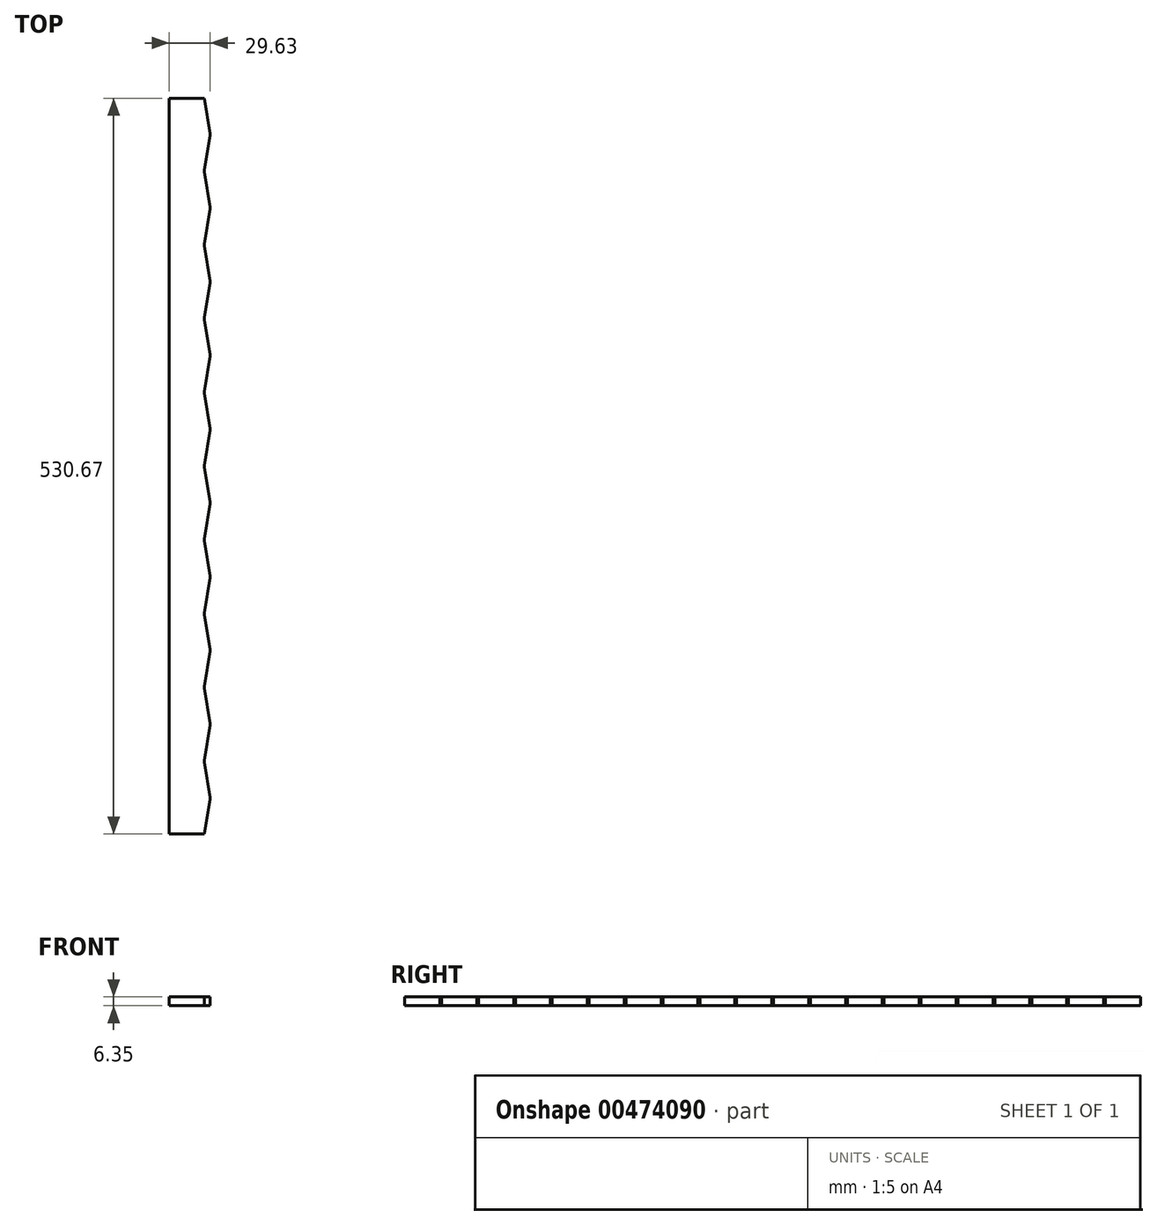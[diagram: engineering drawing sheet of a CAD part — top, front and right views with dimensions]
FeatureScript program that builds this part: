
annotation { "Feature Type Name" : "Feature", "Feature Type Description" : "" }
export const myFeature = defineFeature(function(context is Context, id is Id, definition is map)
    precondition{}
    {
        {
            var Q0;
            Q0=qCreatedBy(makeId("Top.planeOp"),FACE);
            var sketch = newSketch(context, id + "F0", { "sketchPlane" : qUnion([Q0])});
            skLineSegment(sketch, "E0.bottom", {"start": v(0, 0) * mm, "end": v(25.4, 0) * mm});
            skLineSegment(sketch, "E0.top", {"start": v(0, 530.67) * mm, "end": v(25.4, 530.67) * mm});
            skLineSegment(sketch, "E0.left", {"start": v(0, 0) * mm, "end": v(0, 530.67) * mm});
            skLineSegment(sketch, "E0.right", {"start": v(25.4, 0) * mm, "end": v(25.4, 530.67) * mm});
            skLineSegment(sketch, "E1", {"start": v(29.63, 25.3) * mm, "end": v(29.63, 26.6) * mm});
            skLineSegment(sketch, "E2.direction1", {"start": v(25.4, 0) * mm, "end": v(25.4, 51.9) * mm, "construction": true});
            skLineSegment(sketch, "E3", {"start": v(27.52, 39.25) * mm, "end": v(27.52, 12.65) * mm, "construction": true});
            skLineSegment(sketch, "E4", {"start": v(29.63, 25.95) * mm, "end": v(27.52, 25.95) * mm, "construction": true});
            skLineSegment(sketch, "E5", {"start": v(27.52, 25.95) * mm, "end": v(25.4, 25.95) * mm, "construction": true});
            skLineSegment(sketch, "E6", {"start": v(25.4, 51.9) * mm, "end": v(29.63, 26.6) * mm});
            skLineSegment(sketch, "E7", {"start": v(29.63, 25.3) * mm, "end": v(25.4, 0) * mm});
            skLineSegment(sketch, "E8", {"start": v(27.52, 12.65) * mm, "end": v(31.25, 12.03) * mm, "construction": true});
            skLineSegment(sketch, "E9.1.0.0", {"start": v(29.63, 78.5) * mm, "end": v(25.4, 53.2) * mm});
            skLineSegment(sketch, "E9.1.0.1", {"start": v(29.63, 78.5) * mm, "end": v(29.63, 79.8) * mm});
            skLineSegment(sketch, "E9.1.0.2", {"start": v(25.4, 105.1) * mm, "end": v(29.63, 79.8) * mm});
            skLineSegment(sketch, "E9.2.0.0", {"start": v(29.63, 131.7) * mm, "end": v(25.4, 106.4) * mm});
            skLineSegment(sketch, "E9.2.0.1", {"start": v(29.63, 131.7) * mm, "end": v(29.63, 133) * mm});
            skLineSegment(sketch, "E9.2.0.2", {"start": v(25.4, 158.3) * mm, "end": v(29.63, 133) * mm});
            skLineSegment(sketch, "E9.3.0.0", {"start": v(29.63, 184.9) * mm, "end": v(25.4, 159.59) * mm});
            skLineSegment(sketch, "E9.3.0.1", {"start": v(29.63, 184.9) * mm, "end": v(29.63, 186.19) * mm});
            skLineSegment(sketch, "E9.3.0.2", {"start": v(25.4, 211.5) * mm, "end": v(29.63, 186.19) * mm});
            skLineSegment(sketch, "E9.4.0.0", {"start": v(29.63, 238.1) * mm, "end": v(25.4, 212.78) * mm});
            skLineSegment(sketch, "E9.4.0.1", {"start": v(29.63, 238.1) * mm, "end": v(29.63, 239.38) * mm});
            skLineSegment(sketch, "E9.4.0.2", {"start": v(25.4, 264.7) * mm, "end": v(29.63, 239.38) * mm});
            skLineSegment(sketch, "E9.5.0.0", {"start": v(29.63, 291.29) * mm, "end": v(25.4, 265.98) * mm});
            skLineSegment(sketch, "E9.5.0.1", {"start": v(29.63, 291.29) * mm, "end": v(29.63, 292.58) * mm});
            skLineSegment(sketch, "E9.5.0.2", {"start": v(25.4, 317.89) * mm, "end": v(29.63, 292.58) * mm});
            skLineSegment(sketch, "E9.6.0.0", {"start": v(29.63, 344.48) * mm, "end": v(25.4, 319.18) * mm});
            skLineSegment(sketch, "E9.6.0.1", {"start": v(29.63, 344.48) * mm, "end": v(29.63, 345.77) * mm});
            skLineSegment(sketch, "E9.6.0.2", {"start": v(25.4, 371.08) * mm, "end": v(29.63, 345.77) * mm});
            skLineSegment(sketch, "E9.7.0.0", {"start": v(29.63, 397.68) * mm, "end": v(25.4, 372.37) * mm});
            skLineSegment(sketch, "E9.7.0.1", {"start": v(29.63, 397.68) * mm, "end": v(29.63, 398.97) * mm});
            skLineSegment(sketch, "E9.7.0.2", {"start": v(25.4, 424.28) * mm, "end": v(29.63, 398.97) * mm});
            skLineSegment(sketch, "E9.8.0.0", {"start": v(29.63, 450.88) * mm, "end": v(25.4, 425.57) * mm});
            skLineSegment(sketch, "E9.8.0.1", {"start": v(29.63, 450.88) * mm, "end": v(29.63, 452.17) * mm});
            skLineSegment(sketch, "E9.8.0.2", {"start": v(25.4, 477.47) * mm, "end": v(29.63, 452.17) * mm});
            skLineSegment(sketch, "E9.9.0.0", {"start": v(29.63, 504.07) * mm, "end": v(25.4, 478.76) * mm});
            skLineSegment(sketch, "E9.9.0.1", {"start": v(29.63, 504.07) * mm, "end": v(29.63, 505.36) * mm});
            skLineSegment(sketch, "E9.9.0.2", {"start": v(25.4, 530.67) * mm, "end": v(29.63, 505.36) * mm});
            skLineSegment(sketch, "E9.direction1", {"start": v(25.4, 0) * mm, "end": v(25.4, 53.2) * mm, "construction": true});
            skLineSegment(sketch, "E10", {"start": v(27.52, 39.25) * mm, "end": v(27.52, 65.85) * mm, "construction": true});
            skSolve(sketch);
        }
        {
            var Q0;
            Q0 = qSketchRegion(id + "F0", true);
            var Q1;
            {var subQ1=sQuery(id+"F0.wireOp",EDGE,"E0.bottom");Q1=makeQuery(id+"F0.imprint","IMPRINT",FACE,{"disambiguationData":[TD([[makeQuery(id+"F0.imprint","IMPRINT",EDGE,{"derivedFrom":subQ1}),1.0]])]});}
            extrude(context, id + "F1", {"entities" : qUnion([Q0, Q1]), "depth" : 6.35 * mm});
        }
    });
